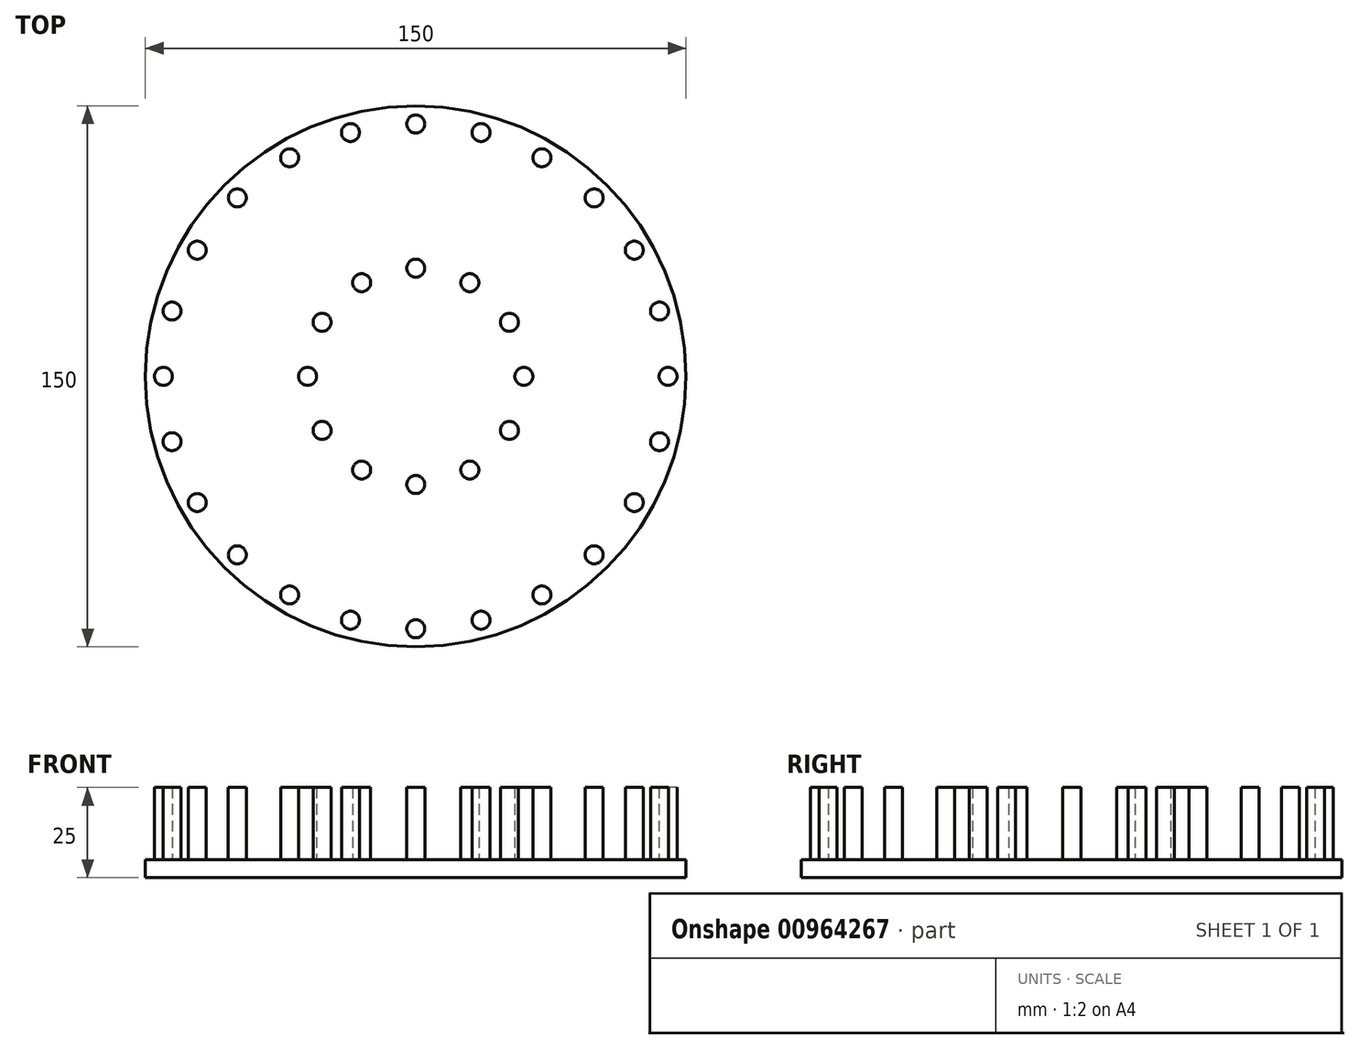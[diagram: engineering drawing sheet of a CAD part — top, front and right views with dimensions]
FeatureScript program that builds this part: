
annotation { "Feature Type Name" : "Feature", "Feature Type Description" : "" }
export const myFeature = defineFeature(function(context is Context, id is Id, definition is map)
    precondition{}
    {
        {
            assignVariable(context, id + "F0", {"name" : "PostHeight", "anyValue" : 20});
        }
        {
            assignVariable(context, id + "F1", {"name" : "SubstrateThickness", "anyValue" : 5});
        }
        {
            var Q0;
            Q0=qCreatedBy(makeId("Top.planeOp"),FACE);
            var sketch = newSketch(context, id + "F2", { "sketchPlane" : qUnion([Q0])});
            skCircle(sketch, "E0", {"center": v(0, 0) * mm, "radius": 75 * mm});
            skSolve(sketch);
        }
        {
            var Q0;
            Q0 = qSketchRegion(id + "F2", true);
            extrude(context, id + "F3", {"entities" : qUnion([Q0]), "endBound" : BoundingType.SYMMETRIC, "depth" : (getVariable(context, 'SubstrateThickness')) * mm, "offsetDistance" : 25 * mm});
        }
        {
            var Q0;
            Q0=makeQuery(id+"F3.opExtrude","CAP_FACE",FACE,{"disambiguationData":[OSD([sQuery(id+"F2.wireOp",EDGE,"E0")])],"isStart":false});
            var sketch = newSketch(context, id + "F4", { "sketchPlane" : qUnion([Q0])});
            skCircle(sketch, "E1", {"center": v(0, 0) * mm, "radius": 70 * mm, "construction": true});
            skCircle(sketch, "E2", {"center": v(0, 0) * mm, "radius": 30 * mm, "construction": true});
            skLineSegment(sketch, "E3", {"start": v(0, 0) * mm, "end": v(0, 70) * mm, "construction": true});
            skPoint(sketch, "E4", {"position": v(0, 30) * mm});
            skLineSegment(sketch, "E5", {"start": v(0, 0) * mm, "end": v(-15, 25.98) * mm, "construction": true});
            skCircle(sketch, "E6", {"center": v(-15, 25.98) * mm, "radius": 2.5 * mm});
            skCircle(sketch, "E7", {"center": v(0, 70) * mm, "radius": 2.5 * mm});
            skCircle(sketch, "E8.1.0", {"center": v(-18.12, 67.61) * mm, "radius": 2.5 * mm});
            skCircle(sketch, "E8.2.0", {"center": v(-35, 60.62) * mm, "radius": 2.5 * mm});
            skCircle(sketch, "E8.3.0", {"center": v(-49.5, 49.5) * mm, "radius": 2.5 * mm});
            skCircle(sketch, "E8.4.0", {"center": v(-60.62, 35) * mm, "radius": 2.5 * mm});
            skCircle(sketch, "E8.5.0", {"center": v(-67.61, 18.12) * mm, "radius": 2.5 * mm});
            skCircle(sketch, "E8.6.0", {"center": v(-70, 0) * mm, "radius": 2.5 * mm});
            skCircle(sketch, "E8.7.0", {"center": v(-67.61, -18.12) * mm, "radius": 2.5 * mm});
            skCircle(sketch, "E8.8.0", {"center": v(-60.62, -35) * mm, "radius": 2.5 * mm});
            skCircle(sketch, "E8.9.0", {"center": v(-49.5, -49.5) * mm, "radius": 2.5 * mm});
            skCircle(sketch, "E8.10.0", {"center": v(-35, -60.62) * mm, "radius": 2.5 * mm});
            skCircle(sketch, "E8.11.0", {"center": v(-18.12, -67.61) * mm, "radius": 2.5 * mm});
            skCircle(sketch, "E8.12.0", {"center": v(0, -70) * mm, "radius": 2.5 * mm});
            skCircle(sketch, "E8.13.0", {"center": v(18.12, -67.61) * mm, "radius": 2.5 * mm});
            skCircle(sketch, "E8.14.0", {"center": v(35, -60.62) * mm, "radius": 2.5 * mm});
            skCircle(sketch, "E8.15.0", {"center": v(49.5, -49.5) * mm, "radius": 2.5 * mm});
            skCircle(sketch, "E8.16.0", {"center": v(60.62, -35) * mm, "radius": 2.5 * mm});
            skCircle(sketch, "E8.17.0", {"center": v(67.61, -18.12) * mm, "radius": 2.5 * mm});
            skCircle(sketch, "E8.18.0", {"center": v(70, 0) * mm, "radius": 2.5 * mm});
            skCircle(sketch, "E8.19.0", {"center": v(67.61, 18.12) * mm, "radius": 2.5 * mm});
            skCircle(sketch, "E8.20.0", {"center": v(60.62, 35) * mm, "radius": 2.5 * mm});
            skCircle(sketch, "E8.21.0", {"center": v(49.5, 49.5) * mm, "radius": 2.5 * mm});
            skCircle(sketch, "E8.22.0", {"center": v(35, 60.62) * mm, "radius": 2.5 * mm});
            skCircle(sketch, "E8.23.0", {"center": v(18.12, 67.61) * mm, "radius": 2.5 * mm});
            skCircle(sketch, "E9.1.0", {"center": v(-25.98, 15) * mm, "radius": 2.5 * mm});
            skCircle(sketch, "E9.2.0", {"center": v(-30, 0) * mm, "radius": 2.5 * mm});
            skCircle(sketch, "E9.3.0", {"center": v(-25.98, -15) * mm, "radius": 2.5 * mm});
            skCircle(sketch, "E9.4.0", {"center": v(-15, -25.98) * mm, "radius": 2.5 * mm});
            skCircle(sketch, "E9.5.0", {"center": v(0, -30) * mm, "radius": 2.5 * mm});
            skCircle(sketch, "E9.6.0", {"center": v(15, -25.98) * mm, "radius": 2.5 * mm});
            skCircle(sketch, "E9.7.0", {"center": v(25.98, -15) * mm, "radius": 2.5 * mm});
            skCircle(sketch, "E9.8.0", {"center": v(30, 0) * mm, "radius": 2.5 * mm});
            skCircle(sketch, "E9.9.0", {"center": v(25.98, 15) * mm, "radius": 2.5 * mm});
            skCircle(sketch, "E9.10.0", {"center": v(15, 25.98) * mm, "radius": 2.5 * mm});
            skCircle(sketch, "E9.11.0", {"center": v(0, 30) * mm, "radius": 2.5 * mm});
            skSolve(sketch);
        }
        {
            var Q0;
            Q0 = qSketchRegion(id + "F4", true);
            extrude(context, id + "F5", {"entities" : qUnion([Q0]), "operationType" : NewBodyOperationType.ADD, "depth" : (getVariable(context, 'PostHeight')) * mm, "offsetDistance" : 25 * mm});
        }
    });
